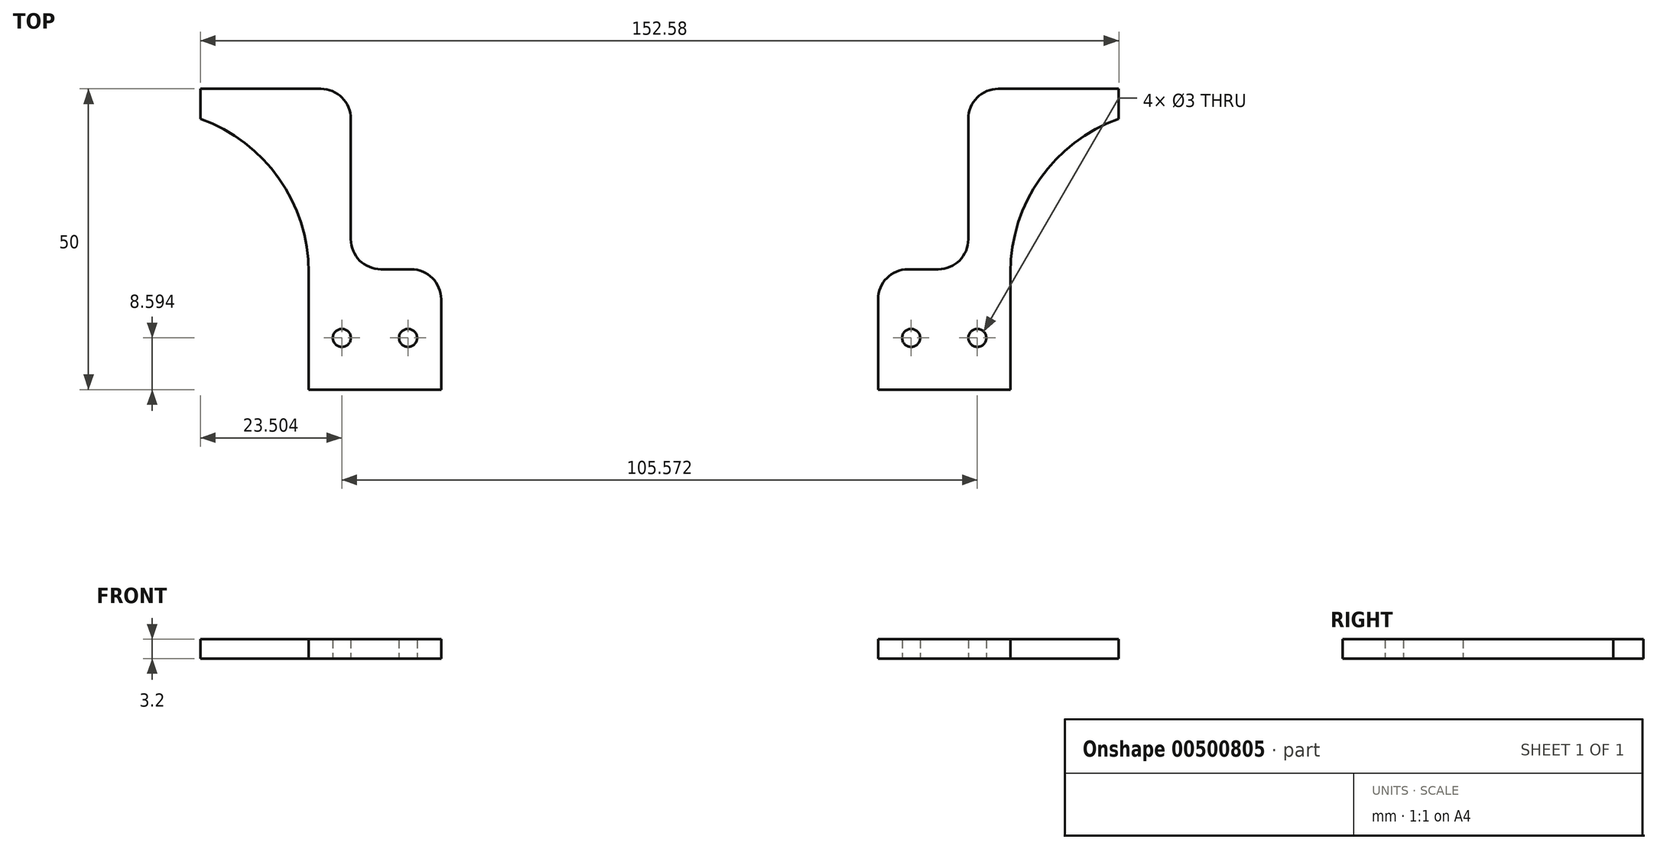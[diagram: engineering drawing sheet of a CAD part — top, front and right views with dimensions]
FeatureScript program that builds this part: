
annotation { "Feature Type Name" : "Feature", "Feature Type Description" : "" }
export const myFeature = defineFeature(function(context is Context, id is Id, definition is map)
    precondition{}
    {
        {
            var Q0;
            Q0=qCreatedBy(makeId("Top.planeOp"),FACE);
            var sketch = newSketch(context, id + "F0", { "sketchPlane" : qUnion([Q0])});
            skLineSegment(sketch, "E0", {"start": v(0, 75.67) * mm, "end": v(0, -74.33) * mm, "construction": true});
            skPoint(sketch, "E1", {"position": v(0, 0) * mm});
            skLineSegment(sketch, "E2", {"start": v(-75, 0) * mm, "end": v(75, 0) * mm, "construction": true});
            skLineSegment(sketch, "E3", {"start": v(0, 0) * mm, "end": v(150, 0) * mm, "construction": true});
            skPoint(sketch, "E4", {"position": v(75, 0) * mm});
            skLineSegment(sketch, "E5", {"start": v(75, 75.67) * mm, "end": v(75, -74.33) * mm, "construction": true});
            skLineSegment(sketch, "E6", {"start": v(51.29, 0) * mm, "end": v(51.29, 30) * mm});
            skLineSegment(sketch, "E7", {"start": v(51.29, 30) * mm, "end": v(76.29, 30) * mm});
            skLineSegment(sketch, "E8", {"start": v(76.29, 30) * mm, "end": v(76.29, 25) * mm});
            skLineSegment(sketch, "E9", {"start": v(58.29, -20) * mm, "end": v(36.29, -20) * mm});
            skLineSegment(sketch, "E10", {"start": v(36.29, -20) * mm, "end": v(36.29, 0) * mm});
            skLineSegment(sketch, "E11", {"start": v(36.29, 0) * mm, "end": v(51.29, 0) * mm});
            skLineSegment(sketch, "E12", {"start": v(58.29, -10) * mm, "end": v(47.29, -10) * mm, "construction": true});
            skLineSegment(sketch, "E13", {"start": v(47.29, 0) * mm, "end": v(47.29, -10) * mm, "construction": true});
            skLineSegment(sketch, "E14", {"start": v(47.29, -10) * mm, "end": v(47.29, -20) * mm, "construction": true});
            skLineSegment(sketch, "E15", {"start": v(47.29, -5) * mm, "end": v(36.29, -5) * mm, "construction": true});
            skLineSegment(sketch, "E16", {"start": v(47.29, -5) * mm, "end": v(58.29, -5) * mm, "construction": true});
            skPoint(sketch, "E17", {"position": v(52.79, -5) * mm});
            skPoint(sketch, "E18", {"position": v(41.79, -5) * mm});
            skLineSegment(sketch, "E19", {"start": v(36.29, -11.4) * mm, "end": v(58.29, -11.4) * mm, "construction": true});
            skCircle(sketch, "E20", {"center": v(41.79, -11.4) * mm, "radius": 1.5 * mm});
            skCircle(sketch, "E21", {"center": v(52.79, -11.4) * mm, "radius": 1.5 * mm});
            skLineSegment(sketch, "E22", {"start": v(58.29, -0.5) * mm, "end": v(58.29, 25) * mm, "construction": true});
            skLineSegment(sketch, "E23", {"start": v(36.29, -10) * mm, "end": v(36.29, -20) * mm});
            skLineSegment(sketch, "E24", {"start": v(36.29, -20) * mm, "end": v(58.29, -20) * mm});
            skLineSegment(sketch, "E25", {"start": v(58.29, -20) * mm, "end": v(58.29, -10) * mm});
            skLineSegment(sketch, "E26", {"start": v(58.29, -10) * mm, "end": v(58.29, -0.5) * mm});
            skCircle(sketch, "E27", {"center": v(41.79, -11.4) * mm, "radius": 4 * mm, "construction": true});
            skPoint(sketch, "E28", {"position": v(47.29, -11.4) * mm});
            skLineSegment(sketch, "E29", {"start": v(52.79, -5) * mm, "end": v(52.79, -11.4) * mm, "construction": true});
            skLineSegment(sketch, "E30", {"start": v(41.79, -5) * mm, "end": v(41.79, -11.4) * mm, "construction": true});
            skArc(sketch, "E31", {"start": v(76.29, 25) * mm, "mid": v(63.24, 15.1) * mm, "end": v(58.29, -0.5) * mm});
            skSolve(sketch);
        }
        {
            var Q0;
            Q0=qSketchRegion(id+"F0",true);
            extrude(context, id + "F1", {"entities" : qUnion([Q0]), "depth" : 3.2 * mm, "offsetDistance" : 25 * mm, "symmetric" : true});
        }
        {
            var Q0;
            Q0=makeQuery(id+"F1.opExtrude","SWEPT_EDGE",EDGE,{"disambiguationData":[OSD([sQuery(id+"F0.wireOp",EDGE,"E6"),sQuery(id+"F0.wireOp",EDGE,"E7")])]});
            var Q1;
            Q1=makeQuery(id+"F1.opExtrude","SWEPT_EDGE",EDGE,{"disambiguationData":[OSD([sQuery(id+"F0.wireOp",EDGE,"E6"),sQuery(id+"F0.wireOp",EDGE,"E11")])]});
            var Q2;
            Q2=makeQuery(id+"F1.opExtrude","SWEPT_EDGE",EDGE,{"disambiguationData":[OSD([sQuery(id+"F0.wireOp",EDGE,"E10"),sQuery(id+"F0.wireOp",EDGE,"E11")])]});
            fillet(context, id + "F2", {"entities" : qUnion([Q0, Q1, Q2]), "radius" : 5 * mm, "tangentPropagation" : true, "allowEdgeOverflow" : false});
        }
        {
            var Q0;
            Q0=makeQuery(id+"F1.opExtrude","SWEPT_BODY",BODY,{"disambiguationData":[OSD([sQuery(id+"F0.wireOp",EDGE,"E6"),sQuery(id+"F0.wireOp",EDGE,"E7"),sQuery(id+"F0.wireOp",EDGE,"E8"),sQuery(id+"F0.wireOp",EDGE,"E10"),sQuery(id+"F0.wireOp",EDGE,"E11"),sQuery(id+"F0.wireOp",EDGE,"E20"),sQuery(id+"F0.wireOp",EDGE,"E21"),sQuery(id+"F0.wireOp",EDGE,"ZwHRgjcJ-jbhn-dUlB-6MDj-OU6wtJwOsmXv"),sQuery(id+"F0.wireOp",EDGE,"E23"),sQuery(id+"F0.wireOp",EDGE,"E24"),sQuery(id+"F0.wireOp",EDGE,"E25"),sQuery(id+"F0.wireOp",EDGE,"E26")])]});
            var Q1;
            Q1=qCreatedBy(makeId("Right.planeOp"),FACE);
            mirror(context, id + "F3", {"entities" : qUnion([Q0]), "mirrorPlane" : qUnion([Q1])});
        }
    });
